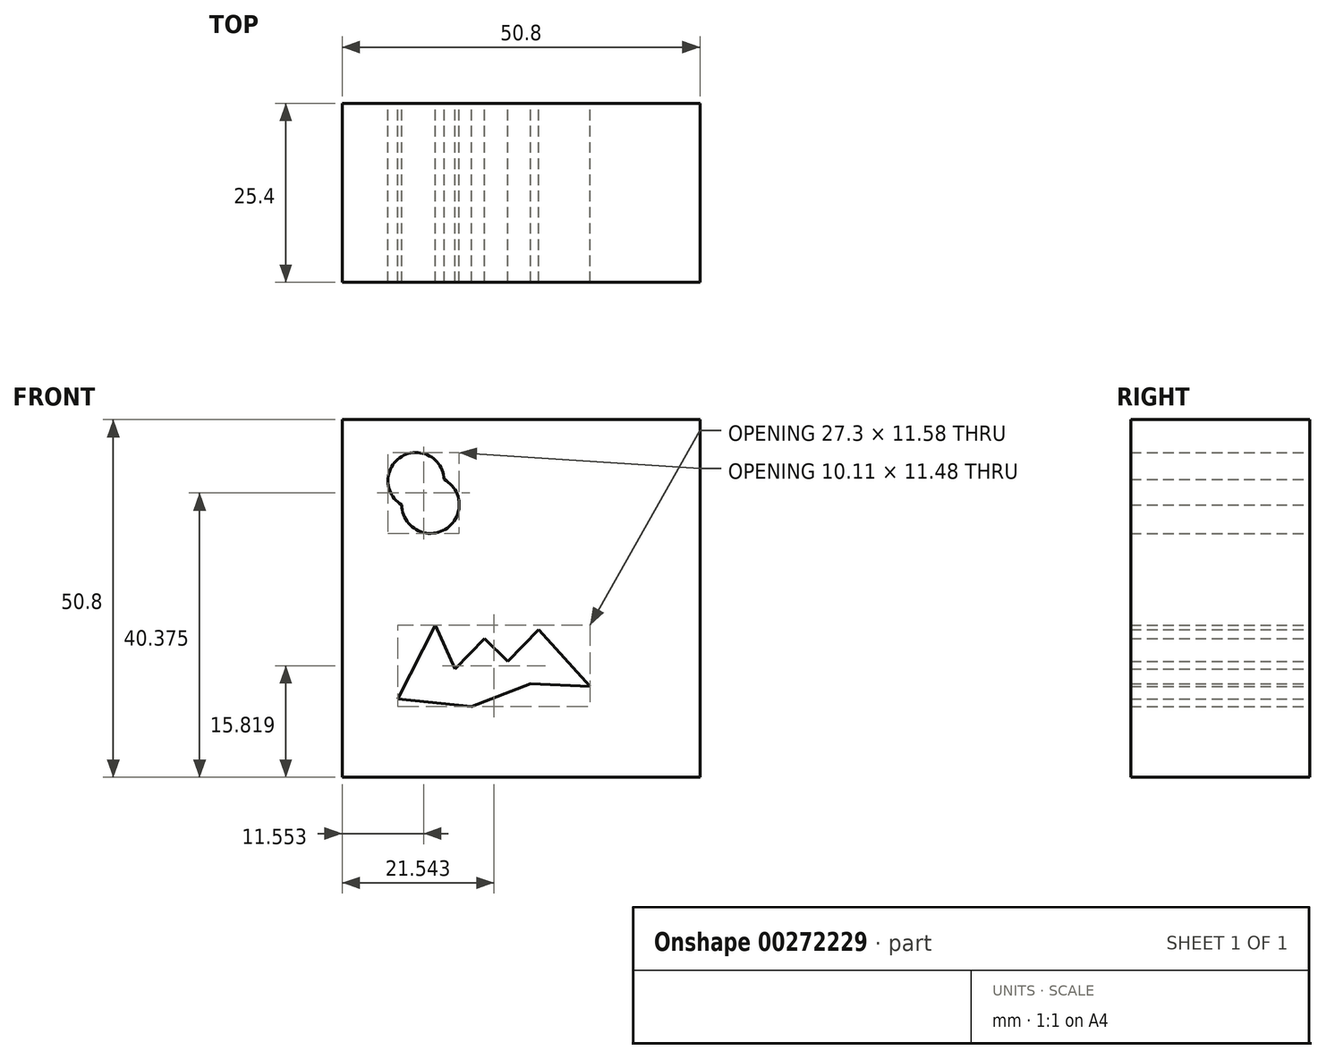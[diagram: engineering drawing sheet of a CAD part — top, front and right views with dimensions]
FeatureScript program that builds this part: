
annotation { "Feature Type Name" : "Feature", "Feature Type Description" : "" }
export const myFeature = defineFeature(function(context is Context, id is Id, definition is map)
    precondition{}
    {
        {
            var Q0;
            Q0=qCreatedBy(makeId("Front.planeOp"),FACE);
            var sketch = newSketch(context, id + "F0", { "sketchPlane" : qUnion([Q0])});
            skLineSegment(sketch, "E0.bottom", {"start": v(-20.21, 35.4) * mm, "end": v(30.59, 35.4) * mm});
            skLineSegment(sketch, "E0.top", {"start": v(-20.21, -15.4) * mm, "end": v(30.59, -15.4) * mm});
            skLineSegment(sketch, "E0.left", {"start": v(-20.21, 35.4) * mm, "end": v(-20.21, -15.4) * mm});
            skLineSegment(sketch, "E0.right", {"start": v(30.59, 35.4) * mm, "end": v(30.59, -15.4) * mm});
            skCircle(sketch, "E1", {"center": v(-9.72, 26.74) * mm, "radius": 3.99 * mm});
            skCircle(sketch, "E2", {"center": v(-7.67, 23.31) * mm, "radius": 4.07 * mm});
            skLineSegment(sketch, "E3", {"start": v(-12.32, -4.3) * mm, "end": v(-6.96, 6.22) * mm});
            skLineSegment(sketch, "E4", {"start": v(-6.96, 6.22) * mm, "end": v(-1.8, -5.36) * mm});
            skLineSegment(sketch, "E5", {"start": v(-1.8, -5.36) * mm, "end": v(-4.2, 0) * mm});
            skLineSegment(sketch, "E6", {"start": v(-4.2, 0) * mm, "end": v(0, 4.3) * mm});
            skLineSegment(sketch, "E7", {"start": v(0, 4.3) * mm, "end": v(6.58, -2.14) * mm});
            skLineSegment(sketch, "E8", {"start": v(3.29, 1.08) * mm, "end": v(7.71, 5.6) * mm});
            skLineSegment(sketch, "E9", {"start": v(7.71, 5.6) * mm, "end": v(14.98, -2.52) * mm});
            skLineSegment(sketch, "E10", {"start": v(-12.32, -4.3) * mm, "end": v(-1.8, -5.36) * mm});
            skLineSegment(sketch, "E11", {"start": v(-1.8, -5.36) * mm, "end": v(6.58, -2.14) * mm});
            skLineSegment(sketch, "E12", {"start": v(6.58, -2.14) * mm, "end": v(14.98, -2.52) * mm});
            skSolve(sketch);
        }
        {
            var Q0;
            Q0 = qSketchRegion(id + "F0", true);
            extrude(context, id + "F1", {"entities" : qUnion([Q0]), "depth" : 25.4 * mm});
        }
    });
